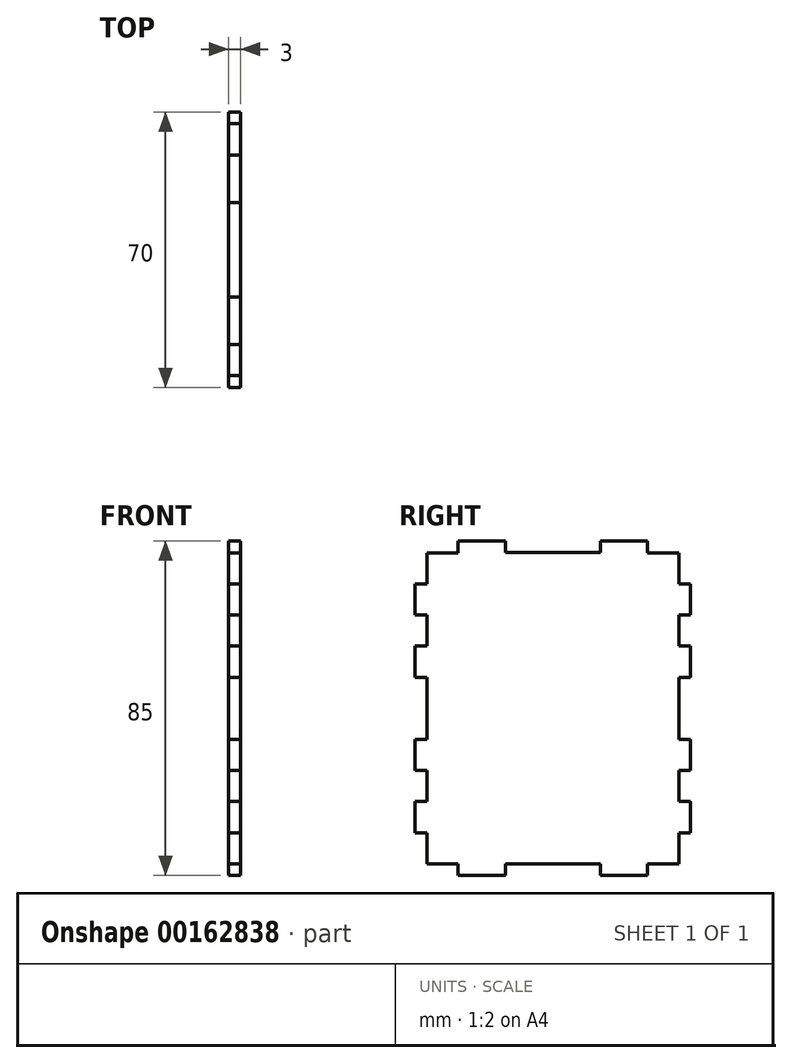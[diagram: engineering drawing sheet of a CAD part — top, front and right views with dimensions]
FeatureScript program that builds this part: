
annotation { "Feature Type Name" : "Feature", "Feature Type Description" : "" }
export const myFeature = defineFeature(function(context is Context, id is Id, definition is map)
    precondition{}
    {
        {
            var Q0;
            Q0=qCreatedBy(makeId("Right.planeOp"),FACE);
            var sketch = newSketch(context, id + "F0", { "sketchPlane" : qUnion([Q0])});
            skLineSegment(sketch, "E0.bottom", {"start": v(-24.1, 42.5) * mm, "end": v(-12.05, 42.5) * mm});
            skLineSegment(sketch, "E0.left", {"start": v(-35, 31.6) * mm, "end": v(-35, 23.7) * mm});
            skLineSegment(sketch, "E1.bottom", {"start": v(-32, 39.5) * mm, "end": v(-24.1, 39.5) * mm});
            skLineSegment(sketch, "E1.left", {"start": v(-32, 39.5) * mm, "end": v(-32, 31.6) * mm});
            skLineSegment(sketch, "E2", {"start": v(-35, 31.6) * mm, "end": v(-32, 31.6) * mm});
            skLineSegment(sketch, "E3", {"start": v(-35, 23.7) * mm, "end": v(-32, 23.7) * mm});
            skLineSegment(sketch, "E4", {"start": v(-35, 15.8) * mm, "end": v(-32, 15.8) * mm});
            skLineSegment(sketch, "E5", {"start": v(-35, 7.9) * mm, "end": v(-32, 7.9) * mm});
            skLineSegment(sketch, "E6", {"start": v(-24.1, 42.5) * mm, "end": v(-24.1, 39.5) * mm});
            skPoint(sketch, "E7.orphan", {"position": v(-35, 42.5) * mm});
            skLineSegment(sketch, "E8.trimOffspring", {"start": v(-35, 15.8) * mm, "end": v(-35, 7.9) * mm});
            skLineSegment(sketch, "E9", {"start": v(0, 39.5) * mm, "end": v(0, 0) * mm});
            skPoint(sketch, "E9.startSnap0", {"position": v(0, 39.5) * mm});
            skPoint(sketch, "E1.right.start.orphan", {"position": v(32, 39.5) * mm});
            skPoint(sketch, "E10.orphan", {"position": v(-32, -39.5) * mm});
            skPoint(sketch, "E11.start.orphan", {"position": v(-35, -31.6) * mm});
            skPoint(sketch, "E12.end.orphan", {"position": v(-32, -23.7) * mm});
            skPoint(sketch, "E13.orphan", {"position": v(-32, -15.8) * mm});
            skPoint(sketch, "E14.start.orphan", {"position": v(-35, -7.9) * mm});
            skPoint(sketch, "E15.orphan", {"position": v(-32, -7.9) * mm});
            skLineSegment(sketch, "E16.trimOffspring", {"start": v(-32, 23.7) * mm, "end": v(-32, 15.8) * mm});
            skLineSegment(sketch, "E17.trimOffspring", {"start": v(-32, 7.9) * mm, "end": v(-32, 0) * mm});
            skLineSegment(sketch, "E18.MirrorCS", {"start": v(24.1, 42.5) * mm, "end": v(24.1, 39.5) * mm});
            skLineSegment(sketch, "E19.MirrorCS", {"start": v(35, 15.8) * mm, "end": v(32, 15.8) * mm});
            skLineSegment(sketch, "E20.MirrorCS", {"start": v(35, 23.7) * mm, "end": v(32, 23.7) * mm});
            skLineSegment(sketch, "E21.MirrorCS", {"start": v(35, 7.9) * mm, "end": v(32, 7.9) * mm});
            skLineSegment(sketch, "E22.MirrorCS", {"start": v(35, 31.6) * mm, "end": v(32, 31.6) * mm});
            skLineSegment(sketch, "E23.MirrorCS", {"start": v(35, 15.8) * mm, "end": v(35, 7.9) * mm});
            skLineSegment(sketch, "E24.MirrorCS", {"start": v(32, 23.7) * mm, "end": v(32, 15.8) * mm});
            skLineSegment(sketch, "E25.MirrorCS", {"start": v(32, 7.9) * mm, "end": v(32, 0) * mm});
            skLineSegment(sketch, "E26.MirrorCS", {"start": v(32, 39.5) * mm, "end": v(32, 31.6) * mm});
            skPoint(sketch, "E27.MirrorP", {"position": v(35, 42.5) * mm});
            skLineSegment(sketch, "E28.MirrorCS", {"start": v(35, 31.6) * mm, "end": v(35, 23.7) * mm});
            skLineSegment(sketch, "E29.MirrorCS", {"start": v(32, 39.5) * mm, "end": v(24.1, 39.5) * mm});
            skLineSegment(sketch, "E30.MirrorCS", {"start": v(24.1, 42.5) * mm, "end": v(12.05, 42.5) * mm});
            skLineSegment(sketch, "E31", {"start": v(-12.05, 42.5) * mm, "end": v(-12.05, 39.57) * mm});
            skLineSegment(sketch, "E32", {"start": v(12.05, 42.5) * mm, "end": v(12.05, 39.57) * mm});
            skPoint(sketch, "E33.orphan", {"position": v(0, 42.5) * mm});
            skLineSegment(sketch, "E34.MirrorCS", {"start": v(35, -23.7) * mm, "end": v(32, -23.7) * mm});
            skLineSegment(sketch, "E35.MirrorCS", {"start": v(-35, -7.9) * mm, "end": v(-32, -7.9) * mm});
            skLineSegment(sketch, "E36.MirrorCS", {"start": v(-35, -23.7) * mm, "end": v(-32, -23.7) * mm});
            skLineSegment(sketch, "E37.MirrorCS", {"start": v(35, -15.8) * mm, "end": v(32, -15.8) * mm});
            skLineSegment(sketch, "E38.MirrorCS", {"start": v(-24.1, -42.5) * mm, "end": v(-24.1, -39.5) * mm});
            skLineSegment(sketch, "E39.MirrorCS", {"start": v(-35, -15.8) * mm, "end": v(-32, -15.8) * mm});
            skLineSegment(sketch, "E40.MirrorCS", {"start": v(35, -7.9) * mm, "end": v(32, -7.9) * mm});
            skLineSegment(sketch, "E41.MirrorCS", {"start": v(24.1, -42.5) * mm, "end": v(24.1, -39.5) * mm});
            skLineSegment(sketch, "E42.MirrorCS", {"start": v(35, -31.6) * mm, "end": v(32, -31.6) * mm});
            skLineSegment(sketch, "E43.MirrorCS", {"start": v(-12.05, -42.5) * mm, "end": v(-12.05, -39.57) * mm});
            skLineSegment(sketch, "E44.MirrorCS", {"start": v(-35, -31.6) * mm, "end": v(-32, -31.6) * mm});
            skPoint(sketch, "E45.MirrorP", {"position": v(0, -39.5) * mm});
            skLineSegment(sketch, "E46.MirrorCS", {"start": v(-32, -39.5) * mm, "end": v(-24.1, -39.5) * mm});
            skPoint(sketch, "E47.MirrorP", {"position": v(0, -42.5) * mm});
            skLineSegment(sketch, "E48.MirrorCS", {"start": v(32, -39.5) * mm, "end": v(32, -31.6) * mm});
            skLineSegment(sketch, "E49.MirrorCS", {"start": v(12.05, -42.5) * mm, "end": v(12.05, -39.57) * mm});
            skLineSegment(sketch, "E50.MirrorCS", {"start": v(32, -7.9) * mm, "end": v(32, 0) * mm});
            skLineSegment(sketch, "E51.MirrorCS", {"start": v(-32, -23.7) * mm, "end": v(-32, -15.8) * mm});
            skLineSegment(sketch, "E52.MirrorCS", {"start": v(-32, -39.5) * mm, "end": v(-32, -31.6) * mm});
            skLineSegment(sketch, "E53.MirrorCS", {"start": v(-35, -31.6) * mm, "end": v(-35, -23.7) * mm});
            skPoint(sketch, "E54.MirrorP", {"position": v(35, -42.5) * mm});
            skLineSegment(sketch, "E55.MirrorCS", {"start": v(-35, -15.8) * mm, "end": v(-35, -7.9) * mm});
            skPoint(sketch, "E56.MirrorP", {"position": v(32, -39.5) * mm});
            skPoint(sketch, "E57.MirrorP", {"position": v(-35, 7.9) * mm});
            skPoint(sketch, "E58.MirrorP", {"position": v(-35, -42.5) * mm});
            skLineSegment(sketch, "E59.MirrorCS", {"start": v(0, -39.5) * mm, "end": v(0, 0) * mm});
            skPoint(sketch, "E60.MirrorP", {"position": v(-32, 7.9) * mm});
            skLineSegment(sketch, "E61.MirrorCS", {"start": v(-32, -7.9) * mm, "end": v(-32, 0) * mm});
            skLineSegment(sketch, "E62.MirrorCS", {"start": v(32, -23.7) * mm, "end": v(32, -15.8) * mm});
            skLineSegment(sketch, "E63.MirrorCS", {"start": v(35, -31.6) * mm, "end": v(35, -23.7) * mm});
            skLineSegment(sketch, "E64.MirrorCS", {"start": v(32, -39.5) * mm, "end": v(24.1, -39.5) * mm});
            skLineSegment(sketch, "E65.MirrorCS", {"start": v(24.1, -42.5) * mm, "end": v(12.05, -42.5) * mm});
            skLineSegment(sketch, "E66.MirrorCS", {"start": v(35, -15.8) * mm, "end": v(35, -7.9) * mm});
            skLineSegment(sketch, "E67.MirrorCS", {"start": v(-24.1, -42.5) * mm, "end": v(-12.05, -42.5) * mm});
            skLineSegment(sketch, "E68", {"start": v(-12.05, 39.57) * mm, "end": v(12.05, 39.57) * mm});
            skPoint(sketch, "E69.orphan", {"position": v(12.05, 39.05) * mm});
            skLineSegment(sketch, "E70", {"start": v(-12.05, -39.57) * mm, "end": v(12.05, -39.57) * mm});
            skPoint(sketch, "E71.orphan", {"position": v(12.05, -39.05) * mm});
            skSolve(sketch);
        }
        {
            var Q0;
            Q0 = qSketchRegion(id + "F0", true);
            extrude(context, id + "F1", {"entities" : qUnion([Q0]), "depth" : 3 * mm});
        }
    });
